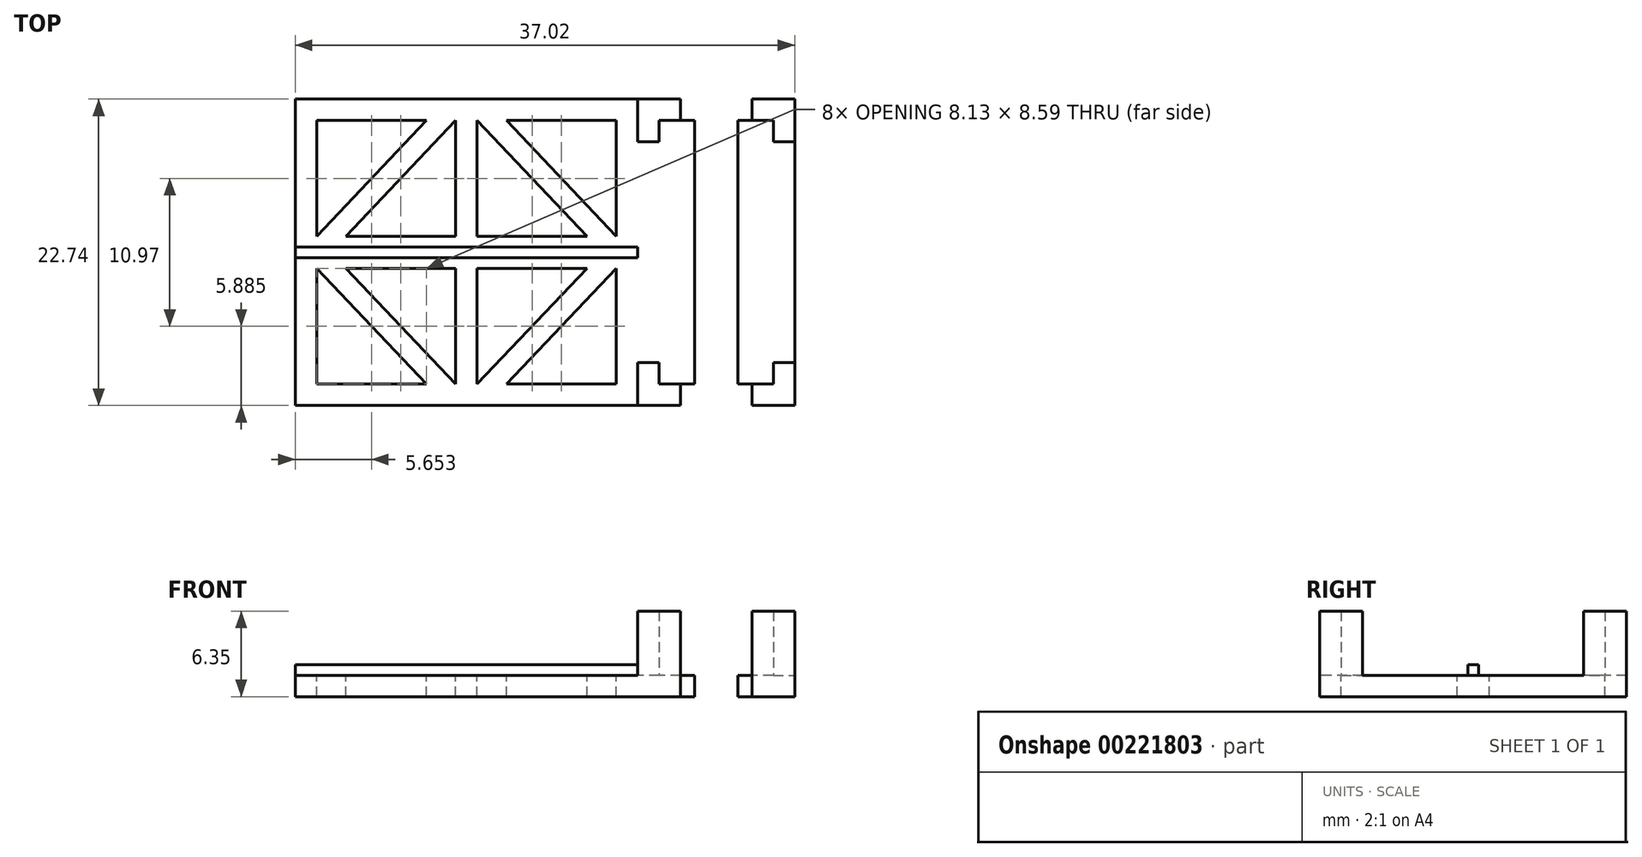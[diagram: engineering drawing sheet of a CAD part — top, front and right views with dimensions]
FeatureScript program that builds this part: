
annotation { "Feature Type Name" : "Feature", "Feature Type Description" : "" }
export const myFeature = defineFeature(function(context is Context, id is Id, definition is map)
    precondition{}
    {
        {
            var Q0;
            Q0=qCreatedBy(makeId("Top.planeOp"),FACE);
            var sketch = newSketch(context, id + "F0", { "sketchPlane" : qUnion([Q0])});
            skLineSegment(sketch, "E0.bottom", {"start": v(3.97, 9.53) * mm, "end": v(-3.97, 9.53) * mm});
            skLineSegment(sketch, "E0.top", {"start": v(3.97, -9.53) * mm, "end": v(-3.97, -9.53) * mm});
            skLineSegment(sketch, "E0.left", {"start": v(3.97, 9.53) * mm, "end": v(3.97, -9.53) * mm});
            skLineSegment(sketch, "E0.right", {"start": v(-3.97, 9.53) * mm, "end": v(-3.97, -9.53) * mm});
            skPoint(sketch, "E0.middle", {"position": v(0, 0) * mm});
            skLineSegment(sketch, "E1.0", {"start": v(4.22, 9.78) * mm, "end": v(-4.22, 9.78) * mm});
            skLineSegment(sketch, "E1.1", {"start": v(4.22, 9.78) * mm, "end": v(4.22, -9.78) * mm});
            skLineSegment(sketch, "E1.2", {"start": v(4.22, -9.78) * mm, "end": v(-4.22, -9.78) * mm});
            skLineSegment(sketch, "E1.3", {"start": v(-4.22, 9.78) * mm, "end": v(-4.22, -9.78) * mm});
            skLineSegment(sketch, "E2.0", {"start": v(5.81, 11.37) * mm, "end": v(-5.81, 11.37) * mm});
            skLineSegment(sketch, "E2.1", {"start": v(5.81, 11.37) * mm, "end": v(5.81, -11.37) * mm});
            skLineSegment(sketch, "E2.2", {"start": v(5.81, -11.37) * mm, "end": v(-5.81, -11.37) * mm});
            skLineSegment(sketch, "E2.3", {"start": v(-5.81, 11.37) * mm, "end": v(-5.81, -11.37) * mm});
            skLineSegment(sketch, "E3.bottom", {"start": v(1.59, -9.78) * mm, "end": v(-1.59, -9.78) * mm});
            skLineSegment(sketch, "E3.top", {"start": v(1.59, 9.78) * mm, "end": v(-1.59, 9.78) * mm});
            skLineSegment(sketch, "E3.left", {"start": v(1.59, -9.78) * mm, "end": v(1.59, 9.78) * mm});
            skLineSegment(sketch, "E3.right", {"start": v(-1.59, -9.78) * mm, "end": v(-1.59, 9.78) * mm});
            skLineSegment(sketch, "E4", {"start": v(-2.64, 11.37) * mm, "end": v(-2.64, 9.78) * mm});
            skLineSegment(sketch, "E5", {"start": v(-5.81, 8.2) * mm, "end": v(-4.22, 8.2) * mm});
            skLineSegment(sketch, "E6", {"start": v(5.81, 8.2) * mm, "end": v(4.22, 8.2) * mm});
            skLineSegment(sketch, "E7", {"start": v(-2.64, -9.78) * mm, "end": v(-2.64, -11.37) * mm});
            skLineSegment(sketch, "E8", {"start": v(4.22, -8.2) * mm, "end": v(5.81, -8.2) * mm});
            skLineSegment(sketch, "E9", {"start": v(-3.97, -8.2) * mm, "end": v(-5.81, -8.2) * mm});
            skPoint(sketch, "E9.endSnap0", {"position": v(-5.81, 0) * mm});
            skLineSegment(sketch, "E10", {"start": v(2.64, -9.78) * mm, "end": v(2.64, -11.37) * mm});
            skLineSegment(sketch, "E11", {"start": v(2.64, 9.78) * mm, "end": v(2.64, 11.37) * mm});
            skLineSegment(sketch, "E12", {"start": v(-5.81, 11.37) * mm, "end": v(-31.21, 11.37) * mm});
            skLineSegment(sketch, "E13", {"start": v(-31.21, 11.37) * mm, "end": v(-31.21, -11.37) * mm});
            skLineSegment(sketch, "E14", {"start": v(-31.21, -11.37) * mm, "end": v(-5.81, -11.37) * mm});
            skPoint(sketch, "E15", {"position": v(-18.51, 0) * mm});
            skPoint(sketch, "E15.positionSnap0", {"position": v(-18.51, 11.37) * mm});
            skLineSegment(sketch, "E16.bottom", {"start": v(-31.21, 0.4) * mm, "end": v(-5.81, 0.4) * mm});
            skLineSegment(sketch, "E16.top", {"start": v(-31.21, -0.4) * mm, "end": v(-5.81, -0.4) * mm});
            skLineSegment(sketch, "E16.left", {"start": v(-31.21, 0.4) * mm, "end": v(-31.21, -0.4) * mm});
            skLineSegment(sketch, "E16.right", {"start": v(-5.81, 0.4) * mm, "end": v(-5.81, -0.4) * mm});
            skLineSegment(sketch, "E17", {"start": v(-29.62, 1.2) * mm, "end": v(-29.62, 9.78) * mm});
            skLineSegment(sketch, "E18", {"start": v(-29.62, 9.78) * mm, "end": v(-21.5, 9.78) * mm});
            skLineSegment(sketch, "E19", {"start": v(-21.5, 9.78) * mm, "end": v(-29.62, 1.2) * mm});
            skLineSegment(sketch, "E20", {"start": v(-19.3, 9.78) * mm, "end": v(-27.44, 1.2) * mm});
            skLineSegment(sketch, "E21", {"start": v(-27.44, 1.2) * mm, "end": v(-19.3, 1.2) * mm});
            skLineSegment(sketch, "E22", {"start": v(-19.3, 1.2) * mm, "end": v(-19.3, 9.78) * mm});
            skLineSegment(sketch, "E23", {"start": v(-18.51, 11.37) * mm, "end": v(-18.51, 0) * mm, "construction": true});
            skLineSegment(sketch, "E24", {"start": v(-31.21, 0) * mm, "end": v(-5.81, 0) * mm, "construction": true});
            skLineSegment(sketch, "E25.MirrorCS", {"start": v(-9.58, 1.2) * mm, "end": v(-17.72, 1.2) * mm});
            skLineSegment(sketch, "E26.MirrorCS", {"start": v(-17.72, 1.2) * mm, "end": v(-17.72, 9.78) * mm});
            skLineSegment(sketch, "E27.MirrorCS", {"start": v(-17.72, 9.78) * mm, "end": v(-9.58, 1.2) * mm});
            skLineSegment(sketch, "E28.MirrorCS", {"start": v(-15.53, 9.78) * mm, "end": v(-7.4, 1.2) * mm});
            skLineSegment(sketch, "E29.MirrorCS", {"start": v(-7.4, 9.78) * mm, "end": v(-15.53, 9.78) * mm});
            skLineSegment(sketch, "E30.MirrorCS", {"start": v(-7.4, 1.2) * mm, "end": v(-7.4, 9.78) * mm});
            skLineSegment(sketch, "E31.MirrorCS", {"start": v(-7.4, -1.2) * mm, "end": v(-7.4, -9.78) * mm});
            skLineSegment(sketch, "E32.MirrorCS", {"start": v(-7.4, -9.78) * mm, "end": v(-15.53, -9.78) * mm});
            skLineSegment(sketch, "E33.MirrorCS", {"start": v(-15.53, -9.78) * mm, "end": v(-7.4, -1.2) * mm});
            skLineSegment(sketch, "E34.MirrorCS", {"start": v(-17.72, -9.78) * mm, "end": v(-9.58, -1.2) * mm});
            skLineSegment(sketch, "E35.MirrorCS", {"start": v(-9.58, -1.2) * mm, "end": v(-17.72, -1.2) * mm});
            skLineSegment(sketch, "E36.MirrorCS", {"start": v(-17.72, -1.2) * mm, "end": v(-17.72, -9.78) * mm});
            skLineSegment(sketch, "E37.MirrorCS", {"start": v(-19.3, -1.2) * mm, "end": v(-19.3, -9.78) * mm});
            skLineSegment(sketch, "E38.MirrorCS", {"start": v(-27.44, -1.2) * mm, "end": v(-19.3, -1.2) * mm});
            skLineSegment(sketch, "E39.MirrorCS", {"start": v(-19.3, -9.78) * mm, "end": v(-27.44, -1.2) * mm});
            skLineSegment(sketch, "E40.MirrorCS", {"start": v(-21.5, -9.78) * mm, "end": v(-29.62, -1.2) * mm});
            skLineSegment(sketch, "E41.MirrorCS", {"start": v(-29.62, -1.2) * mm, "end": v(-29.62, -9.78) * mm});
            skLineSegment(sketch, "E42.MirrorCS", {"start": v(-29.62, -9.78) * mm, "end": v(-21.5, -9.78) * mm});
            skSolve(sketch);
        }
        {
            var Q0;
            {var subQ0=sQuery(id+"F0.wireOp",EDGE,"E3.top");Q0=makeQuery(id+"F0.imprint","IMPRINT",FACE,{"disambiguationData":[TD([[makeQuery(id+"F0.imprint","IMPRINT",EDGE,{"derivedFrom":subQ0}),-1.0]])]});}
            var Q1;
            {var subQ7=sQuery(id+"F0.wireOp",EDGE,"E6");Q1=makeQuery(id+"F0.imprint","IMPRINT",FACE,{"disambiguationData":[TD([[makeQuery(id+"F0.imprint","IMPRINT",EDGE,{"derivedFrom":subQ7}),-1.0]])]});}
            var Q2;
            {var subQ0=sQuery(id+"F0.wireOp",EDGE,"E6");Q2=makeQuery(id+"F0.imprint","IMPRINT",FACE,{"disambiguationData":[TD([[makeQuery(id+"F0.imprint","IMPRINT",EDGE,{"derivedFrom":subQ0}),1.0]])]});}
            var Q3;
            {var subQ7=sQuery(id+"F0.wireOp",EDGE,"E8");Q3=makeQuery(id+"F0.imprint","IMPRINT",FACE,{"disambiguationData":[TD([[makeQuery(id+"F0.imprint","IMPRINT",EDGE,{"derivedFrom":subQ7}),-1.0]])]});}
            var Q4;
            {var subQ0=sQuery(id+"F0.wireOp",EDGE,"E3.bottom");Q4=makeQuery(id+"F0.imprint","IMPRINT",FACE,{"disambiguationData":[TD([[makeQuery(id+"F0.imprint","IMPRINT",EDGE,{"derivedFrom":subQ0}),1.0]])]});}
            var Q5;
            {var subQ3=sQuery(id+"F0.wireOp",EDGE,"E7");Q5=makeQuery(id+"F0.imprint","IMPRINT",FACE,{"disambiguationData":[TD([[makeQuery(id+"F0.imprint","IMPRINT",EDGE,{"derivedFrom":subQ3}),-1.0]])]});}
            var Q6;
            {var subQ0=sQuery(id+"F0.wireOp",EDGE,"E12");Q6=makeQuery(id+"F0.imprint","IMPRINT",FACE,{"disambiguationData":[TD([[makeQuery(id+"F0.imprint","IMPRINT",EDGE,{"derivedFrom":subQ0}),1.0]])]});}
            var Q7;
            {var subQ4=sQuery(id+"F0.wireOp",EDGE,"E4");Q7=makeQuery(id+"F0.imprint","IMPRINT",FACE,{"disambiguationData":[TD([[makeQuery(id+"F0.imprint","IMPRINT",EDGE,{"derivedFrom":subQ4}),-1.0]])]});}
            var Q8;
            {var subQ0=sQuery(id+"F0.wireOp",EDGE,"E5");Q8=makeQuery(id+"F0.imprint","IMPRINT",FACE,{"disambiguationData":[TD([[makeQuery(id+"F0.imprint","IMPRINT",EDGE,{"derivedFrom":subQ0}),-1.0]])]});}
            var Q9;
            {var subQ0=sQuery(id+"F0.wireOp",EDGE,"E0.left");Q9=makeQuery(id+"F0.imprint","IMPRINT",FACE,{"disambiguationData":[TD([[makeQuery(id+"F0.imprint","IMPRINT",EDGE,{"derivedFrom":subQ0}),-1.0]])]});}
            var Q10;
            {var subQ0=sQuery(id+"F0.wireOp",EDGE,"E0.right");var subQ4=sQuery(id+"F0.wireOp",EDGE,"E0.bottom");var subQ5=makeQuery(id+"F0.imprint","INTERSECT",VERTEX,{"derivedFrom":[subQ4,subQ0]});Q10=makeQuery(id+"F0.imprint","IMPRINT",FACE,{"disambiguationData":[TD([[makeQuery(id+"F0.imprint","IMPRINT",EDGE,{"disambiguationData":[TD([[subQ5,1.0]])],"derivedFrom":subQ4}),1.0]])]});}
            var Q11;
            {var subQ6=sQuery(id+"F0.wireOp",EDGE,"E0.right");var subQ7=sQuery(id+"F0.wireOp",EDGE,"E0.bottom");var subQ8=makeQuery(id+"F0.imprint","INTERSECT",VERTEX,{"derivedFrom":[subQ7,subQ6]});Q11=makeQuery(id+"F0.imprint","IMPRINT",FACE,{"disambiguationData":[TD([[makeQuery(id+"F0.imprint","IMPRINT",EDGE,{"disambiguationData":[TD([[subQ8,1.0]])],"derivedFrom":subQ7}),-1.0]])]});}
            var Q12;
            {var subQ4=sQuery(id+"F0.wireOp",EDGE,"E0.right");var subQ5=sQuery(id+"F0.wireOp",EDGE,"E0.top");var subQ6=makeQuery(id+"F0.imprint","INTERSECT",VERTEX,{"derivedFrom":[subQ5,subQ4]});Q12=makeQuery(id+"F0.imprint","IMPRINT",FACE,{"disambiguationData":[TD([[makeQuery(id+"F0.imprint","IMPRINT",EDGE,{"disambiguationData":[TD([[subQ6,1.0]])],"derivedFrom":subQ5}),1.0]])]});}
            var Q13;
            {var subQ9=sQuery(id+"F0.wireOp",EDGE,"E0.left");Q13=makeQuery(id+"F0.imprint","IMPRINT",FACE,{"disambiguationData":[TD([[makeQuery(id+"F0.imprint","IMPRINT",EDGE,{"derivedFrom":subQ9}),1.0]])]});}
            var Q14;
            {var subQ0=sQuery(id+"F0.wireOp",EDGE,"E14");Q14=makeQuery(id+"F0.imprint","IMPRINT",FACE,{"disambiguationData":[TD([[makeQuery(id+"F0.imprint","IMPRINT",EDGE,{"derivedFrom":subQ0}),1.0]])]});}
            var Q15;
            Q15=makeQuery(id+"F0.imprint","IMPRINT",FACE,{"disambiguationData":[TD([[makeQuery(id+"F0.imprint","IMPRINT",EDGE,{"derivedFrom":sQuery(id+"F0.wireOp",EDGE,"E16.bottom")}),-1.0]])]});
            var Q16;
            Q16=sQuery(id+"F0.wireOp",EDGE,"E12");
            var Q17;
            Q17=sQuery(id+"F0.wireOp",EDGE,"E13");
            var Q18;
            Q18=sQuery(id+"F0.wireOp",EDGE,"E14");
            var Q19;
            Q19=sQuery(id+"F0.wireOp",EDGE,"E2.2");
            var Q20;
            Q20=sQuery(id+"F0.wireOp",EDGE,"E2.1");
            var Q21;
            Q21=sQuery(id+"F0.wireOp",EDGE,"E2.0");
            extrude(context, id + "F1", {"entities" : qUnion([Q0, Q1, Q2, Q3, Q4, Q5, Q6, Q7, Q8, Q9, Q10, Q11, Q12, Q13, Q14, Q15]), "surfaceEntities" : qUnion([Q16, Q17, Q18, Q19, Q20, Q21]), "oppositeDirection" : true, "depth" : 1.59 * mm});
        }
        {
            var Q0;
            {var subQ4=sQuery(id+"F0.wireOp",EDGE,"E4");Q0=makeQuery(id+"F0.imprint","IMPRINT",FACE,{"disambiguationData":[TD([[makeQuery(id+"F0.imprint","IMPRINT",EDGE,{"derivedFrom":subQ4}),-1.0]])]});}
            var Q1;
            {var subQ7=sQuery(id+"F0.wireOp",EDGE,"E6");Q1=makeQuery(id+"F0.imprint","IMPRINT",FACE,{"disambiguationData":[TD([[makeQuery(id+"F0.imprint","IMPRINT",EDGE,{"derivedFrom":subQ7}),-1.0]])]});}
            var Q2;
            {var subQ7=sQuery(id+"F0.wireOp",EDGE,"E8");Q2=makeQuery(id+"F0.imprint","IMPRINT",FACE,{"disambiguationData":[TD([[makeQuery(id+"F0.imprint","IMPRINT",EDGE,{"derivedFrom":subQ7}),-1.0]])]});}
            var Q3;
            {var subQ3=sQuery(id+"F0.wireOp",EDGE,"E7");Q3=makeQuery(id+"F0.imprint","IMPRINT",FACE,{"disambiguationData":[TD([[makeQuery(id+"F0.imprint","IMPRINT",EDGE,{"derivedFrom":subQ3}),-1.0]])]});}
            extrude(context, id + "F2", {"entities" : qUnion([Q0, Q1, Q2, Q3]), "operationType" : NewBodyOperationType.ADD, "depth" : 4.76 * mm});
        }
        {
            var Q0;
            Q0=makeQuery(id+"F0.imprint","IMPRINT",FACE,{"disambiguationData":[TD([[makeQuery(id+"F0.imprint","IMPRINT",EDGE,{"derivedFrom":sQuery(id+"F0.wireOp",EDGE,"E16.bottom")}),-1.0]])]});
            extrude(context, id + "F3", {"entities" : qUnion([Q0]), "operationType" : NewBodyOperationType.ADD, "depth" : 0.8 * mm});
        }
    });
